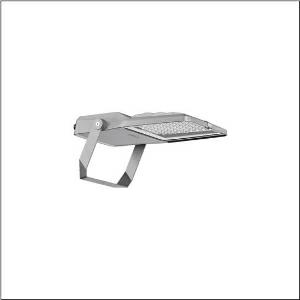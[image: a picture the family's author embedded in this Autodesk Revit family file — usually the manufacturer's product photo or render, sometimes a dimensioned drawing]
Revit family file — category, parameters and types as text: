
# Revit family: floodlight_fl_21_mini___pl43_5xa7772b1a1a_f20f
name_source: partatom
category: Lighting Fixtures
units: mm (PartAtom-declared; Revit-internal decimal feet)

## family parameters
Cut with Voids When Loaded = No
Host = Face
Light Source = No
Part Type = Normal
Room Calculation Point = No
Round Connector Dimension = Use Diameter
Shared = No

## types (1)
- --- (1 x LED, 5300 lm, 45.5 W, 2200K)
    Apparent Load = 46 VA
    CIE Flux Codes = 27 78 99 100 100
    Color Rendering = 70
    Color Temperature = 2200K
    Default Elevation = 1800 mm
    Description = Floodlight FL 21 mini, floodlight, primary light control with lens, of PMMA, primary optical cover: protective disc, of toughened safety glass, transparent, light distribution: PL43, light emission: direct distribution, installation type: surface-mounted, LED, High Power LED, rated luminous flux: 5.300lm, luminous efficacy: 116lm/W, light colour: 722, colour temperature: 2200K, control gear: ECG iQ, control: Street-Remote, Auto-Match, Temp-Guard, Night-Set, Smart-Wire, Desk-Remote (wireless, voltage-free reading and setting of iQ features in the workshop via application-optimized NFC function/RFID function), optimised constant luminous flux control (CLO 2.0), with terminal, 6-pole, mains connection: 220..240V, AC, 50/60Hz, start of lifetime: 46W, end of lifetime: 48W, reduction: 21W, luminaire housing, of diecast aluminium, powder-coated, Siteco® metallic grey (DB 702S), corrosivity category C5 according to DIN EN ISO 12944, mounting bracket, of steel, galvanised, powder-coated, Siteco® metallic grey (DB 702S), protection rating (complete): IP66, insulation class (complete): insulation class II (safety insulation), certification: CE, ENEC, VDE, protection symbol: D, impact resistance: IK08, permissible operating ambient temperature: -40..+40°C, permissible operating ambient temperature for outdoor applications: -40..+50°C, standard: DIN EN 12944, packaging unit: 1 piece

Light Distribution: PL43
    Height = 70 mm
    Lamp = 1 x LED
    Lamp Light Flux = 5300 lm
    Lamp Power = 45.5 W
    Lamp count = 1
    Length = 485 mm
    Luminous efficacy = 116 lm/W
    Manufacturer = Siteco
    ModVariant = No
    Model = 5XA7772B1A1A
    Number of Poles = 1
    OnlyDefault = Yes
    Power Factor = 1
    Product Name = Floodlight FL 21 mini | PL43
    Product group = floodlight | pylon top
    ProductGroupID = 6101
    Protection Class = Protection class II
    Protection Degree = IP 66
    RLX_Detail_Level = 1
    RlxData = <blob elided: 96081 chars, md5=7f6f9cdd>
    Socket = socket
    Standby Power = 0 W
    System Light Flux = 5300 lm
    System Power = 46 W
    Type Comments = factory setting: luminous flux: 100 % | dim-lin: 254 | 463 mA
    Type Image = l_1006845.jpg
    URL = http://relux.com
    VarID = @adj_074049
    Voltage = 0 V
    Weight = 0.00 kg
    Width = 337 mm

## geometry (parser evidence)
native form markers: Blend x4, Sweep x12
no freeform markers — native parametric forms only
